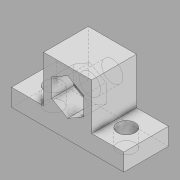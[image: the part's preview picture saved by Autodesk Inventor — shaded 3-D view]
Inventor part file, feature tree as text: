
AUTODESK INVENTOR PART (.ipt)
format: ipt  version: 2020 (Build 240168000, 168)  size: 134,656 bytes
history: native  units: in
note: dims shown in document units (in); Inventor stores cm internally (conversion verified against a paired STEP export)
features: extrude x4, projected_geometry x4, sketch x3
ambient origin geometry x8: Origin, YZ Plane, XZ Plane, XY Plane, X Axis, Y Axis, Z Axis, Center Point
bodies: Solid1 (feature_tree)
feature tree (11):
  extrude  "Extrusion1"  Depth=0.573in
  sketch  "Sketch2"  dims[d6=0.378in d7=0.0in d8=0.0in]
  extrude  "Extrusion2"  TaperAngle=0.0deg  [1 undecoded]
  extrude  "Extrusion3"  Depth=0.4in
  extrude  "Extrusion4"  Depth=0.4in
  sketch  "Sketch1"  dims[d3=0.8in d4=0.0in d5=0.573in]
  projected_geometry  "Projected Loop1"
  sketch  "Sketch3"  dims[d9=0.4in d10=0.0in d11=0.315in d15=1.3in d16=0.0in d17=0.0in]
  projected_geometry  "Projected Loop2"
  projected_geometry  "Projected Loop3"
  projected_geometry  "Projected Loop4"
note: 1 required parameter value undecoded (feature->parameter linkage not recoverable at this tier; creation-order binding heuristic only, values carry confidence <= 0.55)
